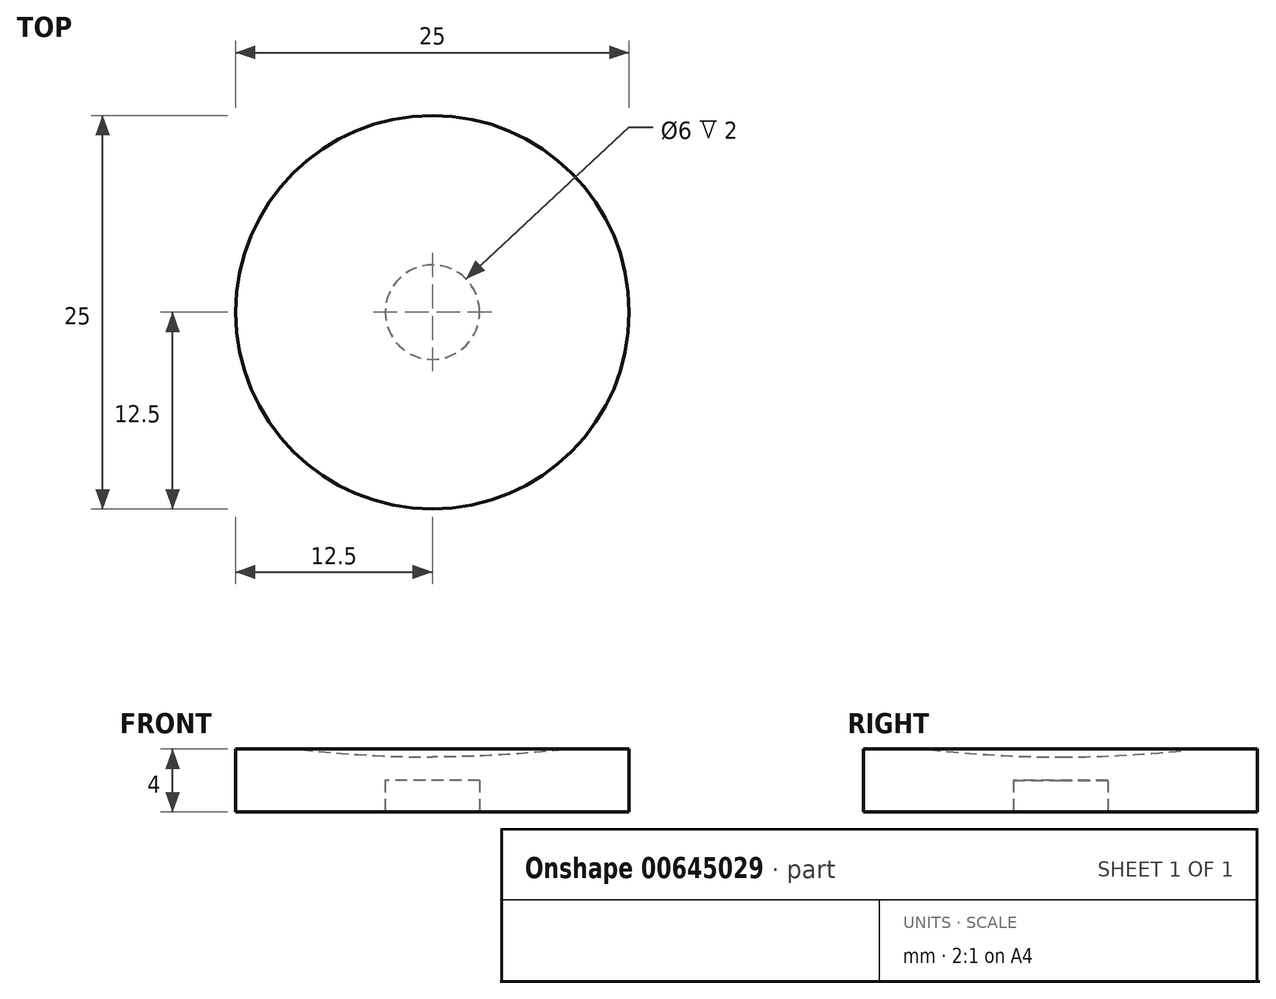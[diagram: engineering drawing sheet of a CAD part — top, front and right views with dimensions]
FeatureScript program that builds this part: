
annotation { "Feature Type Name" : "Feature", "Feature Type Description" : "" }
export const myFeature = defineFeature(function(context is Context, id is Id, definition is map)
    precondition{}
    {
        {
            var Q0;
            Q0=qCreatedBy(makeId("Top.planeOp"),FACE);
            var sketch = newSketch(context, id + "F0", { "sketchPlane" : qUnion([Q0])});
            skCircle(sketch, "E0", {"center": v(0, 0) * mm, "radius": 3 * mm});
            skCircle(sketch, "E1", {"center": v(0, 0) * mm, "radius": 12.5 * mm});
            skSolve(sketch);
        }
        {
            var Q0;
            Q0 = qSketchRegion(id + "F0", true);
            var Q1;
            Q1=makeQuery(id+"F0.imprint","IMPRINT",FACE,{"disambiguationData":[TD([[makeQuery(id+"F0.imprint","IMPRINT",EDGE,{"derivedFrom":sQuery(id+"F0.wireOp",EDGE,"E0")}),1.0]])]});
            extrude(context, id + "F1", {"entities" : qUnion([Q0, Q1]), "depth" : 4 * mm, "offsetDistance" : 25 * mm});
        }
        {
            var Q0;
            Q0=makeQuery(id+"F0.imprint","IMPRINT",FACE,{"disambiguationData":[TD([[makeQuery(id+"F0.imprint","IMPRINT",EDGE,{"derivedFrom":sQuery(id+"F0.wireOp",EDGE,"E0")}),1.0]])]});
            extrude(context, id + "F2", {"entities" : qUnion([Q0]), "operationType" : NewBodyOperationType.REMOVE, "depth" : 2 * mm, "offsetDistance" : 25 * mm});
        }
        {
            var Q0;
            Q0=qCreatedBy(makeId("Front.planeOp"),FACE);
            var sketch = newSketch(context, id + "F3", { "sketchPlane" : qUnion([Q0])});
            skLineSegment(sketch, "E2", {"start": v(0, 0) * mm, "end": v(0, 4) * mm});
            skLineSegment(sketch, "E3", {"start": v(-13.82, 3.5) * mm, "end": v(12.12, 3.5) * mm});
            skCircle(sketch, "E4", {"center": v(0, 78.5) * mm, "radius": 75 * mm});
            skLineSegment(sketch, "E5", {"start": v(0, 4) * mm, "end": v(0, 161.27) * mm});
            skSolve(sketch);
        }
        {
            var Q0;
            {var subQ0=sQuery(id+"F3.wireOp",EDGE,"E5");var subQ1=sQuery(id+"F3.wireOp",EDGE,"E2");var subQ2=makeQuery(id+"F3.imprint","INTERSECT",VERTEX,{"derivedFrom":[subQ1,subQ0]});Q0=makeQuery(id+"F3.imprint","IMPRINT",FACE,{"disambiguationData":[TD([[makeQuery(id+"F3.imprint","IMPRINT",EDGE,{"disambiguationData":[TD([[subQ2,1.0]])],"derivedFrom":subQ1}),1.0]])]});}
            var Q1;
            Q1=sQuery(id+"F3.wireOp",EDGE,"E5");
            revolve(context, id + "F4", {"operationType" : NewBodyOperationType.REMOVE, "entities" : qUnion([Q0]), "axis" : qUnion([Q1]), "revolveType" : RevolveType.FULL});
        }
        {
            var Q0;
            Q0=makeQuery(id+"F4.boolean.opBoolean","INTERSECT",EDGE,{"derivedFrom":[makeQuery(id+"F1.opExtrude","CAP_FACE",FACE,{"disambiguationData":[OSD([sQuery(id+"F0.wireOp",EDGE,"E1")])],"isStart":false}),makeQuery(id+"F4.opRevolve","SWEPT_FACE",FACE,{"disambiguationData":[OSD([sQuery(id+"F3.wireOp",EDGE,"E4")])]})]});
            fillet(context, id + "F5", {"entities" : qUnion([Q0]), "radius" : 5 * mm, "tangentPropagation" : true, "allowEdgeOverflow" : false});
        }
    });
